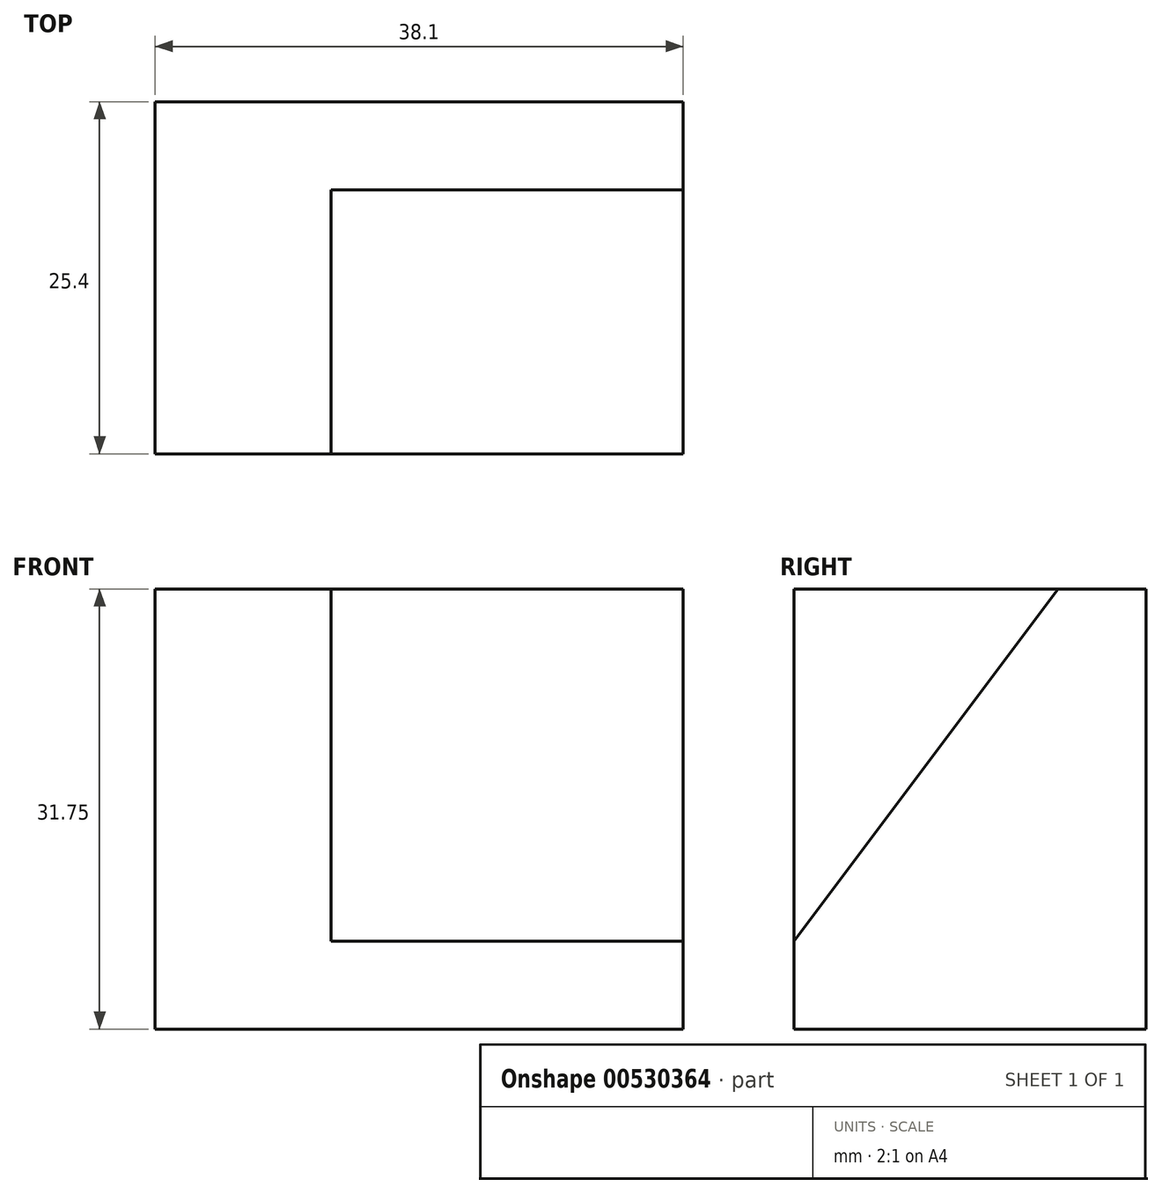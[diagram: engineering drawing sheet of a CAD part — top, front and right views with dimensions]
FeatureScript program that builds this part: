
annotation { "Feature Type Name" : "Feature", "Feature Type Description" : "" }
export const myFeature = defineFeature(function(context is Context, id is Id, definition is map)
    precondition{}
    {
        {
            var Q0;
            Q0=qCreatedBy(makeId("Front.planeOp"),FACE);
            var sketch = newSketch(context, id + "F0", { "sketchPlane" : qUnion([Q0])});
            skLineSegment(sketch, "E0", {"start": v(-38.1, 0) * mm, "end": v(0, 0) * mm});
            skLineSegment(sketch, "E1", {"start": v(0, 0) * mm, "end": v(0, 31.75) * mm});
            skLineSegment(sketch, "E2", {"start": v(0, 31.75) * mm, "end": v(-38.1, 31.75) * mm});
            skLineSegment(sketch, "E3", {"start": v(-38.1, 31.75) * mm, "end": v(-38.1, 0) * mm});
            skSolve(sketch);
        }
        {
            var Q0;
            Q0 = qSketchRegion(id + "F0", true);
            extrude(context, id + "F1", {"entities" : qUnion([Q0]), "depth" : 25.4 * mm, "offsetDistance" : 25.4 * mm});
        }
        {
            var Q0;
            Q0=qCreatedBy(makeId("Right.planeOp"),FACE);
            var sketch = newSketch(context, id + "F2", { "sketchPlane" : qUnion([Q0])});
            skLineSegment(sketch, "E4", {"start": v(-6.35, 31.77) * mm, "end": v(-25.4, 6.35) * mm});
            skLineSegment(sketch, "E5", {"start": v(-25.4, 6.35) * mm, "end": v(-25.4, 31.75) * mm});
            skLineSegment(sketch, "E6", {"start": v(-25.4, 31.75) * mm, "end": v(-6.35, 31.77) * mm});
            skSolve(sketch);
        }
        {
            var Q0;
            Q0=makeQuery(id+"F2.imprint","IMPRINT",FACE,{"disambiguationData":[TD([[makeQuery(id+"F2.imprint","IMPRINT",EDGE,{"derivedFrom":sQuery(id+"F2.wireOp",EDGE,"E4")}),-1.0]])]});
            extrude(context, id + "F3", {"entities" : qUnion([Q0]), "operationType" : NewBodyOperationType.REMOVE, "oppositeDirection" : true, "depth" : 25.4 * mm, "offsetDistance" : 25.4 * mm});
        }
    });
